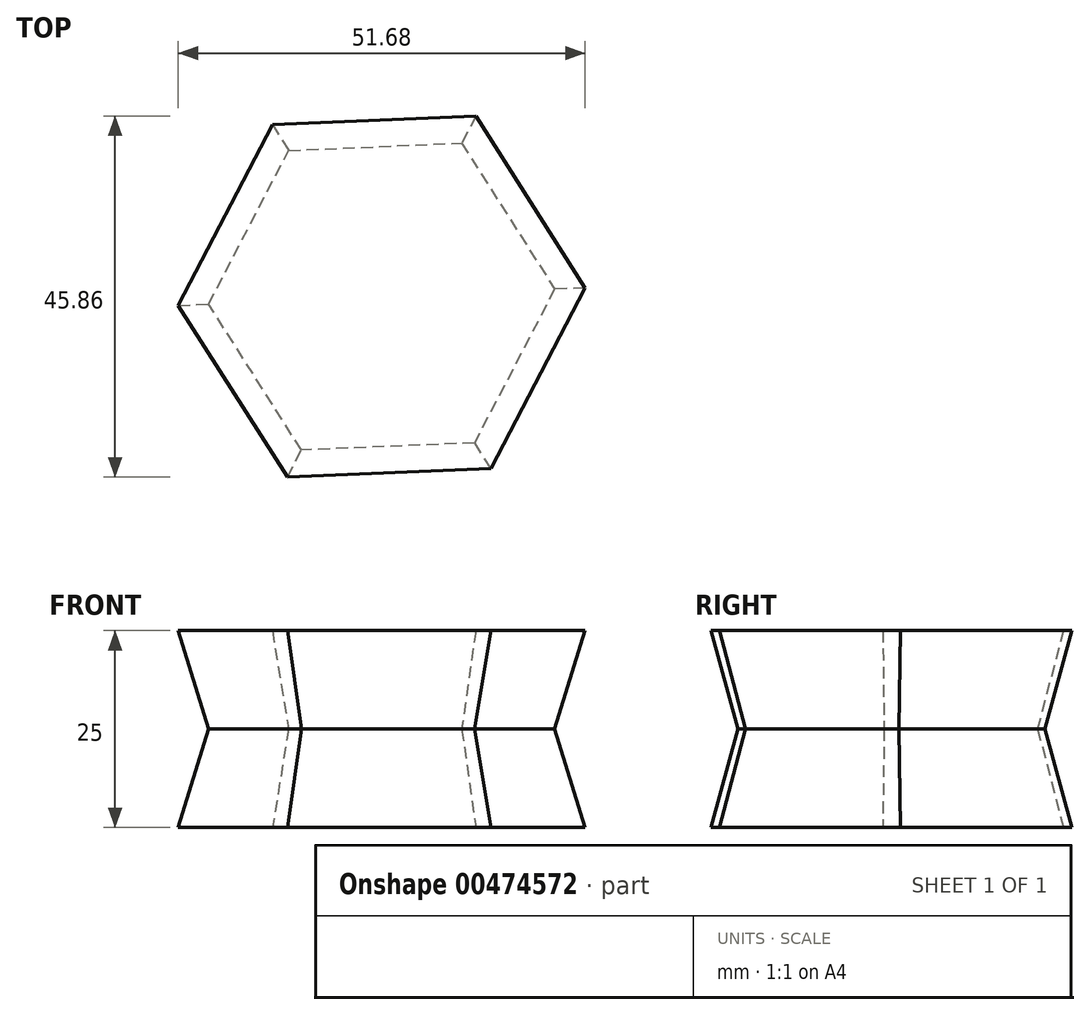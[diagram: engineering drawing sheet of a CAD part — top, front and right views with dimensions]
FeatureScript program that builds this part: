
annotation { "Feature Type Name" : "Feature", "Feature Type Description" : "" }
export const myFeature = defineFeature(function(context is Context, id is Id, definition is map)
    precondition{}
    {
        {
            var Q0;
            Q0=qCreatedBy(makeId("Top.planeOp"),FACE);
            var sketch = newSketch(context, id + "F0", { "sketchPlane" : qUnion([Q0])});
            skCircle(sketch, "E0.cCircle", {"center": v(-19.16, 46.55) * mm, "radius": 19.05 * mm, "construction": true});
            skLineSegment(sketch, "E0.0", {"start": v(-8.98, 66.05) * mm, "end": v(2.82, 47.49) * mm});
            skLineSegment(sketch, "E0.1", {"start": v(2.82, 47.49) * mm, "end": v(-7.36, 27.98) * mm});
            skLineSegment(sketch, "E0.2", {"start": v(-7.36, 27.98) * mm, "end": v(-29.34, 27.04) * mm});
            skLineSegment(sketch, "E0.3", {"start": v(-29.34, 27.04) * mm, "end": v(-41.14, 45.61) * mm});
            skLineSegment(sketch, "E0.4", {"start": v(-41.14, 45.61) * mm, "end": v(-30.96, 65.12) * mm});
            skLineSegment(sketch, "E0.5", {"start": v(-30.96, 65.12) * mm, "end": v(-8.98, 66.05) * mm});
            skPoint(sketch, "E0.0.midPoint", {"position": v(-3.08, 56.77) * mm});
            skSolve(sketch);
        }
        {
            var Q0;
            Q0 = qSketchRegion(id + "F0", true);
            extrude(context, id + "F1", {"entities" : qUnion([Q0]), "depth" : 25 * mm, "hasDraft" : true, "draftAngle" : 15 * degree, "symmetric" : true});
        }
    });
